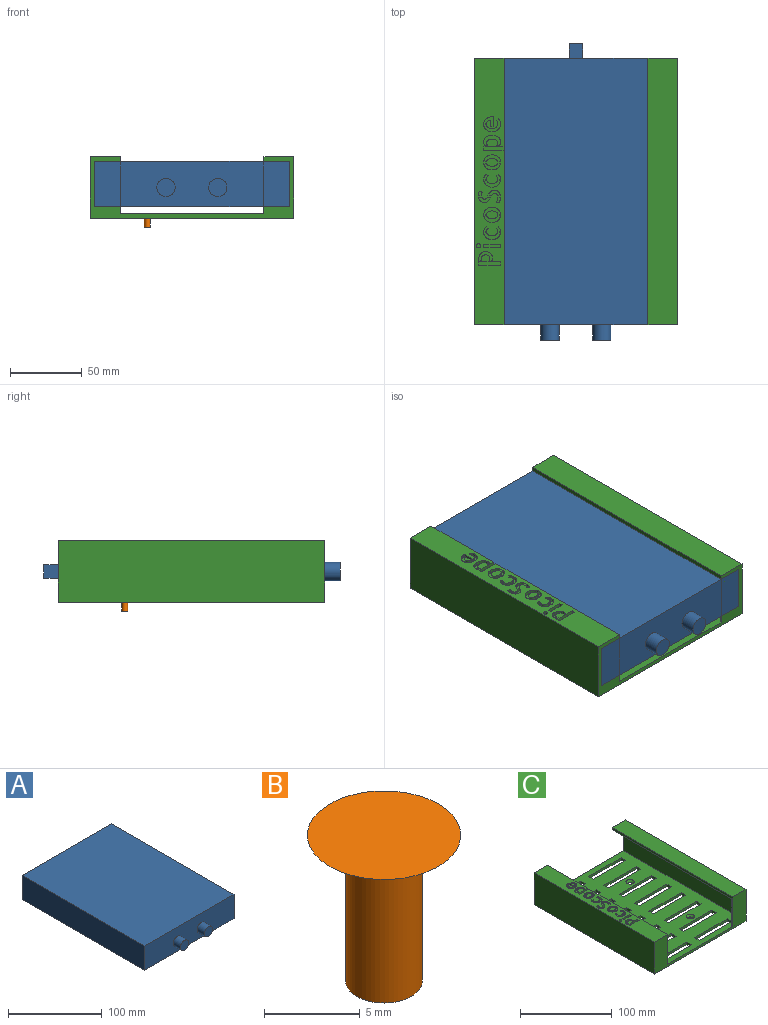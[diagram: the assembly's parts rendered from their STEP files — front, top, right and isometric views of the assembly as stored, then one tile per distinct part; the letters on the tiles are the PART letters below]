
ASSEMBLY  parts=3 mates=5
PART A: 23 faces, bbox 135x205.8x36.5 mm
  f0: plane 185x31.5mm, normal (1,0,0), area 5827.5mm2, adj f1,f3,f4,f18
  f1: plane 135x31.5mm, normal (0,1,0), area 4162.2mm2, adj f0,f2,f4,f9,f10,f11,f12,f18
  f2: plane 185x31.5mm, normal (-1,0,0), area 5827.5mm2, adj f1,f3,f4,f18
  f3: plane 135x31.5mm, normal (0,-1,0), area 3999.1mm2, adj f0,f2,f4,f5,f7,f18
  f4: plane 185x135mm, normal (0,0,1), area 24975mm2, adj f0,f1,f2,f3
  f5: cylinder r=6.35mm len=12.7mm, axis (0,1,0), area 430.9mm2, adj f3,f6
  f6: plane 12.7x12.7mm, normal (0,-1,0), area 126.7mm2, adj f5
  f7: cylinder r=6.35mm len=12.7mm, axis (0,1,0), area 430.9mm2, adj f3,f8
  f8: plane 12.7x12.7mm, normal (0,-1,0), area 126.7mm2, adj f7
  f9: plane 10x9.5mm, normal (-1,0,0), area 95mm2, adj f1,f10,f12,f13
  f10: plane 10x9.5mm, normal (0,0,1), area 95mm2, adj f1,f9,f11,f13
  f11: plane 10x9.5mm, normal (1,0,0), area 95mm2, adj f1,f10,f12,f13
  f12: plane 10x9.5mm, normal (0,0,-1), area 95mm2, adj f1,f9,f11,f13
  f13: plane 9.5x9.5mm, normal (0,1,0), area 90.2mm2, adj f9,f10,f11,f12
  f14: cylinder r=5mm len=10mm, axis (0,0,-1), area 157.1mm2, adj f18,f21
  f15: cylinder r=5mm len=10mm, axis (0,0,-1), area 157.1mm2, adj f18,f20
  f16: cylinder r=5mm len=10mm, axis (0,0,-1), area 157.1mm2, adj f18,f19
  f17: cylinder r=5mm len=10mm, axis (0,0,-1), area 157.1mm2, adj f18,f22
  f18: plane 185x135mm, normal (0,0,-1), area 24660.8mm2, adj f0,f1,f2,f3,f14,f15,f16,f17
  f19: plane 10x10mm, normal (0,0,-1), area 78.5mm2, adj f16
  f20: plane 10x10mm, normal (0,0,-1), area 78.5mm2, adj f15
  f21: plane 10x10mm, normal (0,0,-1), area 78.5mm2, adj f14
  f22: plane 10x10mm, normal (0,0,-1), area 78.5mm2, adj f17
PART B: 4 faces, bbox 8x8x9.3 mm
  f0: plane 8x8mm, normal (0,0,1), area 50.3mm2, adj f1
  f1: cone r=4mm half-angle=57deg, axis (0,0,1), area 45mm2, adj f0,f2
  f2: cylinder r=2mm len=8mm, axis (0,0,1), area 100.5mm2, adj f1,f3
  f3: plane 4x4mm, normal (0,0,-1), area 12.6mm2, adj f2
PART C: 385 faces, bbox 141.1x185x42.5 mm
  f0: plane 185x135.1mm, normal (0,0,1), area 19106.2mm2, adj f1,f4,f9,f11,f12,f13,f14,f15
  f1: plane 185x39.5mm, normal (1,0,0), area 586.5mm2, adj f0,f2,f5,f12,f13,f282,f285,f286
  f2: plane 185x20.55mm, normal (0,0,1), area 3302.4mm2, adj f1,f6,f12,f13,f78,f79,f80,f81
  f3: plane 185x141.1mm, normal (0,0,-1), area 20439.9mm2, adj f6,f7,f12,f13,f14,f15,f16,f17
  f4: plane 184x36.5mm, normal (1,0,0), area 6716mm2, adj f0,f5,f12,f383
  f5: plane 184x17.55mm, normal (0,0,-1), area 3229.2mm2, adj f1,f4,f12,f383
  f6: plane 185x42.5mm, normal (-1,0,0), area 7862.5mm2, adj f2,f3,f12,f13
  f7: plane 185x42.5mm, normal (1,0,0), area 7862.5mm2, adj f3,f8,f12,f13
  f8: plane 185x20.55mm, normal (0,0,1), area 3801.7mm2, adj f7,f9,f12,f13
  f9: plane 185x39.5mm, normal (-1,0,0), area 591.5mm2, adj f0,f8,f10,f12,f13,f384
  f10: plane 184x17.55mm, normal (0,0,-1), area 3229.2mm2, adj f9,f11,f12,f384
  f11: plane 184x36.5mm, normal (-1,0,0), area 6716mm2, adj f0,f10,f12,f384
  f12: plane 141.1x42.5mm, normal (0,1,0), area 765.6mm2, adj f0,f1,f2,f3,f4,f5,f6,f7
  f13: plane 141.1x42.5mm, normal (0,-1,0), area 2046.7mm2, adj f0,f1,f2,f3,f6,f7,f8,f9
  f14: plane 50x3mm, normal (0,-1,0), area 150mm2, adj f0,f3,f15,f16
  f15: plane 7x3mm, normal (1,0,0), area 21mm2, adj f0,f3,f14,f17
  f16: plane 7x3mm, normal (-1,0,0), area 21mm2, adj f0,f3,f14,f17
  f17: plane 50x3mm, normal (0,1,0), area 150mm2, adj f0,f3,f15,f16
  f18: plane 50x3mm, normal (0,1,0), area 150mm2, adj f0,f3,f19,f21
  f19: plane 7x3mm, normal (1,0,0), area 21mm2, adj f0,f3,f18,f20
  f20: plane 50x3mm, normal (0,-1,0), area 150mm2, adj f0,f3,f19,f21
  f21: plane 7x3mm, normal (-1,0,0), area 21mm2, adj f0,f3,f18,f20
  f22: plane 7x3mm, normal (-1,0,0), area 21mm2, adj f0,f3,f23,f24
  f23: plane 50x3mm, normal (0,-1,0), area 150mm2, adj f0,f3,f22,f25
  f24: plane 50x3mm, normal (0,1,0), area 150mm2, adj f0,f3,f22,f25
  f25: plane 7x3mm, normal (1,0,0), area 21mm2, adj f0,f3,f23,f24
  f26: plane 50x3mm, normal (0,1,0), area 150mm2, adj f0,f3,f27,f29
  f27: plane 7x3mm, normal (1,0,0), area 21mm2, adj f0,f3,f26,f28
  f28: plane 50x3mm, normal (0,-1,0), area 150mm2, adj f0,f3,f27,f29
  f29: plane 7x3mm, normal (-1,0,0), area 21mm2, adj f0,f3,f26,f28
  f30: plane 50x3mm, normal (0,-1,0), area 150mm2, adj f0,f3,f31,f32
  f31: plane 7x3mm, normal (1,0,0), area 21mm2, adj f0,f3,f30,f33
  f32: plane 7x3mm, normal (-1,0,0), area 21mm2, adj f0,f3,f30,f33
  f33: plane 50x3mm, normal (0,1,0), area 150mm2, adj f0,f3,f31,f32
  f34: plane 7x3mm, normal (-1,0,0), area 21mm2, adj f0,f3,f35,f36
  f35: plane 50x3mm, normal (0,-1,0), area 150mm2, adj f0,f3,f34,f37
  f36: plane 50x3mm, normal (0,1,0), area 150mm2, adj f0,f3,f34,f37
  f37: plane 7x3mm, normal (1,0,0), area 21mm2, adj f0,f3,f35,f36
  f38: plane 50x3mm, normal (0,1,0), area 150mm2, adj f0,f3,f39,f41
  f39: plane 7x3mm, normal (1,0,0), area 21mm2, adj f0,f3,f38,f40
  f40: plane 50x3mm, normal (0,-1,0), area 150mm2, adj f0,f3,f39,f41
  f41: plane 7x3mm, normal (-1,0,0), area 21mm2, adj f0,f3,f38,f40
  f42: plane 7x3mm, normal (-1,0,0), area 21mm2, adj f0,f3,f43,f44
  f43: plane 50x3mm, normal (0,-1,0), area 150mm2, adj f0,f3,f42,f45
  f44: plane 50x3mm, normal (0,1,0), area 150mm2, adj f0,f3,f42,f45
  f45: plane 7x3mm, normal (1,0,0), area 21mm2, adj f0,f3,f43,f44
  f46: plane 50x3mm, normal (0,-1,0), area 150mm2, adj f0,f3,f47,f48
  f47: plane 7x3mm, normal (1,0,0), area 21mm2, adj f0,f3,f46,f49
  f48: plane 7x3mm, normal (-1,0,0), area 21mm2, adj f0,f3,f46,f49
  f49: plane 50x3mm, normal (0,1,0), area 150mm2, adj f0,f3,f47,f48
  f50: plane 50x3mm, normal (0,-1,0), area 150mm2, adj f0,f3,f51,f52
  f51: plane 7x3mm, normal (1,0,0), area 21mm2, adj f0,f3,f50,f53
  f52: plane 7x3mm, normal (-1,0,0), area 21mm2, adj f0,f3,f50,f53
  f53: plane 50x3mm, normal (0,1,0), area 150mm2, adj f0,f3,f51,f52
  f54: plane 50x3mm, normal (0,-1,0), area 150mm2, adj f0,f3,f55,f56
  f55: plane 7x3mm, normal (1,0,0), area 21mm2, adj f0,f3,f54,f57
  f56: plane 7x3mm, normal (-1,0,0), area 21mm2, adj f0,f3,f54,f57
  f57: plane 50x3mm, normal (0,1,0), area 150mm2, adj f0,f3,f55,f56
  f58: plane 50x3mm, normal (0,-1,0), area 150mm2, adj f0,f3,f59,f60
  f59: plane 7x3mm, normal (1,0,0), area 21mm2, adj f0,f3,f58,f61
  f60: plane 7x3mm, normal (-1,0,0), area 21mm2, adj f0,f3,f58,f61
  f61: plane 50x3mm, normal (0,1,0), area 150mm2, adj f0,f3,f59,f60
  f62: plane 50x3mm, normal (0,-1,0), area 150mm2, adj f0,f3,f63,f64
  f63: plane 7x3mm, normal (1,0,0), area 21mm2, adj f0,f3,f62,f65
  f64: plane 7x3mm, normal (-1,0,0), area 21mm2, adj f0,f3,f62,f65
  f65: plane 50x3mm, normal (0,1,0), area 150mm2, adj f0,f3,f63,f64
  f66: plane 7x3mm, normal (1,0,0), area 21mm2, adj f0,f3,f67,f68
  f67: plane 50x3mm, normal (0,1,0), area 150mm2, adj f0,f3,f66,f69
  f68: plane 50x3mm, normal (0,-1,0), area 150mm2, adj f0,f3,f66,f69
  f69: plane 7x3mm, normal (-1,0,0), area 21mm2, adj f0,f3,f67,f68
  f70: plane 7x3mm, normal (1,0,0), area 21mm2, adj f0,f3,f71,f72
  f71: plane 50x3mm, normal (0,1,0), area 150mm2, adj f0,f3,f70,f73
  f72: plane 50x3mm, normal (0,-1,0), area 150mm2, adj f0,f3,f70,f73
  f73: plane 7x3mm, normal (-1,0,0), area 21mm2, adj f0,f3,f71,f72
  f74: plane 7x3mm, normal (1,0,0), area 21mm2, adj f0,f3,f75,f76
  f75: plane 50x3mm, normal (0,1,0), area 150mm2, adj f0,f3,f74,f77
  f76: plane 50x3mm, normal (0,-1,0), area 150mm2, adj f0,f3,f74,f77
  f77: plane 7x3mm, normal (-1,0,0), area 21mm2, adj f0,f3,f75,f76
  f78: extruded ~2.2x2mm, area 4.5mm2, adj f2,f79,f93,f94
  f79: extruded ~2.2x2mm, area 4.5mm2, adj f2,f78,f80,f94
  f80: extruded ~2x1.81mm, area 4.1mm2, adj f2,f79,f81,f94
  f81: extruded ~2x1.53mm, area 4mm2, adj f2,f80,f82,f94
  f82: extruded ~2.02x2mm, area 4.2mm2, adj f2,f81,f83,f94
  f83: plane 2x1.95mm, normal (0,-1,0), area 3.9mm2, adj f2,f82,f84,f94
  f84: extruded ~2x0.95mm, area 2.1mm2, adj f2,f83,f85,f94
  f85: extruded ~2x0.88mm, area 2.3mm2, adj f2,f84,f86,f94
  f86: extruded ~2x1.2mm, area 2.6mm2, adj f2,f85,f87,f94
  f87: extruded ~2x1.42mm, area 2.9mm2, adj f2,f86,f88,f94
  f88: extruded ~2.55x2mm, area 5.3mm2, adj f2,f87,f89,f94
  f89: extruded ~2x1.63mm, area 4.3mm2, adj f2,f88,f90,f94
  f90: plane 2x1.89mm, normal (0,-1,0), area 3.8mm2, adj f2,f89,f91,f94
  f91: extruded ~2x1.98mm, area 4.1mm2, adj f2,f90,f92,f94
  f92: extruded ~2x1.54mm, area 4mm2, adj f2,f91,f93,f94
  f93: extruded ~2x1.78mm, area 4.1mm2, adj f2,f78,f92,f94
  f94: plane 11.6x4.84mm, normal (0,0,1), area 30.6mm2, adj f78,f79,f80,f81,f82,f83,f84,f85
  f95: extruded ~2.03x2mm, area 4.2mm2, adj f2,f96,f110,f111
  f96: plane 2x1.91mm, normal (0,1,0), area 3.8mm2, adj f2,f95,f97,f111
  f97: extruded ~2x0.96mm, area 2.1mm2, adj f2,f96,f98,f111
  f98: extruded ~2x0.87mm, area 2.3mm2, adj f2,f97,f99,f111
  f99: extruded ~2x1.19mm, area 2.6mm2, adj f2,f98,f100,f111
  f100: extruded ~2x1.41mm, area 2.9mm2, adj f2,f99,f101,f111
  f101: extruded ~2.54x2mm, area 5.3mm2, adj f2,f100,f102,f111
  f102: extruded ~2x1.66mm, area 4.3mm2, adj f2,f101,f103,f111
  f103: plane 2x1.95mm, normal (0,1,0), area 3.9mm2, adj f2,f102,f104,f111
  f104: extruded ~2x1.99mm, area 4.2mm2, adj f2,f103,f105,f111
  f105: extruded ~2x1.55mm, area 4mm2, adj f2,f104,f106,f111
  f106: extruded ~2x1.79mm, area 4.1mm2, adj f2,f105,f107,f111
  f107: extruded ~2.21x2mm, area 4.5mm2, adj f2,f106,f108,f111
  f108: extruded ~2.22x2mm, area 4.5mm2, adj f2,f107,f109,f111
  f109: extruded ~2x1.82mm, area 4.1mm2, adj f2,f108,f110,f111
  f110: extruded ~2x1.54mm, area 4mm2, adj f2,f95,f109,f111
  f111: plane 11.62x4.88mm, normal (0,0,1), area 30.9mm2, adj f95,f96,f97,f98,f99,f100,f101,f102
  f112: extruded ~2.18x2mm, area 4.4mm2, adj f2,f113,f127,f128
  f113: extruded ~2.2x2mm, area 4.5mm2, adj f2,f112,f114,f128
  f114: extruded ~2x1.82mm, area 4.1mm2, adj f2,f113,f115,f128
  f115: extruded ~2x1.53mm, area 4mm2, adj f2,f114,f116,f128
  f116: extruded ~2.02x2mm, area 4.2mm2, adj f2,f115,f117,f128
  f117: plane 2.02x2mm, normal (0,-1,0), area 4mm2, adj f2,f116,f118,f128
  f118: extruded ~2x0.95mm, area 2.1mm2, adj f2,f117,f119,f128
  f119: extruded ~2x0.85mm, area 2.2mm2, adj f2,f118,f120,f128
  f120: extruded ~2x1.17mm, area 2.5mm2, adj f2,f119,f121,f128
  f121: extruded ~2x1.41mm, area 2.8mm2, adj f2,f120,f122,f128
  f122: extruded ~2.49x2mm, area 5.2mm2, adj f2,f121,f123,f128
  f123: extruded ~2x1.63mm, area 4.2mm2, adj f2,f122,f124,f128
  f124: plane 2x1.98mm, normal (0,-1,0), area 4mm2, adj f2,f123,f125,f128
  f125: extruded ~2x1.98mm, area 4.2mm2, adj f2,f124,f126,f128
  f126: extruded ~2x1.54mm, area 4mm2, adj f2,f125,f127,f128
  f127: extruded ~2x1.79mm, area 4.1mm2, adj f2,f112,f126,f128
  f128: plane 11.6x4.84mm, normal (0,0,1), area 30.9mm2, adj f112,f113,f114,f115,f116,f117,f118,f119
  f129: extruded ~2x1.25mm, area 2.6mm2, adj f2,f130,f134,f135
  f130: plane 2.02x2mm, normal (0,1,0), area 4mm2, adj f2,f129,f131,f135
  f131: extruded ~2x1.79mm, area 3.7mm2, adj f2,f130,f132,f135
  f132: extruded ~2x1.36mm, area 3.7mm2, adj f2,f131,f133,f135
  f133: plane 2x1.32mm, normal (0.57,-0.82,0), area 3.2mm2, adj f2,f132,f134,f135
  f134: extruded ~2x0.99mm, area 2.4mm2, adj f2,f129,f133,f135
  f135: plane 3.15x3.01mm, normal (0,0,1), area 5.8mm2, adj f129,f130,f131,f132,f133,f134
  f136: extruded ~2x1.89mm, area 3.9mm2, adj f2,f137,f157,f158
  f137: plane 2x1.04mm, normal (1,0,0), area 2.1mm2, adj f2,f136,f138,f158
  f138: plane 2x1.85mm, normal (0,1,0), area 3.7mm2, adj f2,f137,f139,f158
  f139: plane 2x1mm, normal (-1,0,0), area 2mm2, adj f2,f138,f140,f158
  f140: extruded ~2x1.51mm, area 3.1mm2, adj f2,f139,f141,f158
  f141: extruded ~2x0.89mm, area 2.3mm2, adj f2,f140,f142,f158
  f142: extruded ~2x0.91mm, area 2mm2, adj f2,f141,f143,f158
  f143: extruded ~2x0.85mm, area 1.7mm2, adj f2,f142,f144,f158
  f144: extruded ~2x1.54mm, area 3.1mm2, adj f2,f143,f145,f158
  f145: extruded ~2x0.97mm, area 2.3mm2, adj f2,f144,f146,f158
  f146: extruded ~2x0.8mm, area 1.9mm2, adj f2,f145,f147,f158
  f147: extruded ~2x0.89mm, area 1.8mm2, adj f2,f146,f148,f158
  f148: plane 2x1.4mm, normal (1,0,0), area 2.8mm2, adj f2,f147,f149,f158
  f149: plane 2x1.79mm, normal (0,1,0), area 3.6mm2, adj f2,f148,f150,f158
  f150: plane 2x0.98mm, normal (-1,0,0), area 2mm2, adj f2,f149,f151,f158
  f151: extruded ~2.16x2mm, area 4.4mm2, adj f2,f150,f152,f158
  f152: extruded ~2x1.67mm, area 3.9mm2, adj f2,f151,f153,f158
  f153: extruded ~2x1.56mm, area 3.8mm2, adj f2,f152,f154,f158
  f154: extruded ~2.06x2mm, area 4.2mm2, adj f2,f153,f155,f158
  f155: extruded ~2x1.95mm, area 4mm2, adj f2,f154,f156,f158
  f156: extruded ~2x1.47mm, area 3.8mm2, adj f2,f155,f157,f158
  f157: extruded ~2x1.68mm, area 3.8mm2, adj f2,f136,f156,f158
  f158: plane 9.58x6.27mm, normal (0,0,1), area 29.6mm2, adj f136,f137,f138,f139,f140,f141,f142,f143
  f159: plane 2.48x2mm, normal (-1,0,0), area 5mm2, adj f2,f160,f162,f163
  f160: plane 11.47x2mm, normal (0,-1,0), area 22.9mm2, adj f2,f159,f161,f163
  f161: plane 2.48x2mm, normal (1,0,0), area 5mm2, adj f2,f160,f162,f163
  f162: plane 11.47x2mm, normal (0,1,0), area 22.9mm2, adj f2,f159,f161,f163
  f163: plane 11.47x2.48mm, normal (0,0,1), area 28.5mm2, adj f159,f160,f161,f162
  f164: extruded ~2x1.03mm, area 2.3mm2, adj f2,f165,f171,f172
  f165: extruded ~2x1.04mm, area 2.3mm2, adj f2,f164,f166,f172
  f166: extruded ~2x1.04mm, area 2.3mm2, adj f2,f165,f167,f172
  f167: extruded ~2x1.02mm, area 2.3mm2, adj f2,f166,f168,f172
  f168: extruded ~2x1.04mm, area 2.3mm2, adj f2,f167,f169,f172
  f169: extruded ~2x1.02mm, area 2.3mm2, adj f2,f168,f170,f172
  f170: extruded ~2x1.03mm, area 2.3mm2, adj f2,f169,f171,f172
  f171: extruded ~2x1.04mm, area 2.3mm2, adj f2,f164,f170,f172
  f172: plane 2.91x2.91mm, normal (0,0,1), area 6.7mm2, adj f164,f165,f166,f167,f168,f169,f170,f171
  f173: extruded ~2x0.84mm, area 2.2mm2, adj f2,f174,f178,f179
  f174: plane 2x1.32mm, normal (-0.64,-0.77,0), area 3.4mm2, adj f2,f173,f175,f179
  f175: extruded ~2x1.46mm, area 3.8mm2, adj f2,f174,f176,f179
  f176: extruded ~2x1.92mm, area 4mm2, adj f2,f175,f177,f179
  f177: plane 2x1.95mm, normal (0,1,0), area 3.9mm2, adj f2,f176,f178,f179
  f178: extruded ~2x1.44mm, area 3mm2, adj f2,f173,f177,f179
  f179: plane 3.38x3.01mm, normal (0,0,1), area 6mm2, adj f173,f174,f175,f176,f177,f178
  f180: extruded ~2x1.37mm, area 3mm2, adj f2,f181,f192,f193
  f181: plane 2.38x2mm, normal (0,1,0), area 4.8mm2, adj f2,f180,f182,f193
  f182: extruded ~2x1.2mm, area 3mm2, adj f2,f181,f183,f193
  f183: extruded ~2x1.18mm, area 2.6mm2, adj f2,f182,f184,f193
  f184: extruded ~2.22x2mm, area 6.1mm2, adj f2,f183,f185,f193
  f185: plane 2x1.95mm, normal (0,1,0), area 3.9mm2, adj f2,f184,f186,f193
  f186: extruded ~2x1.67mm, area 3.5mm2, adj f2,f185,f187,f193
  f187: extruded ~2x1.23mm, area 3.1mm2, adj f2,f186,f188,f193
  f188: extruded ~2x1.25mm, area 3mm2, adj f2,f187,f189,f193
  f189: extruded ~2x1.42mm, area 2.9mm2, adj f2,f188,f190,f193
  f190: extruded ~2x1.77mm, area 3.6mm2, adj f2,f189,f191,f193
  f191: extruded ~2x1.21mm, area 3.1mm2, adj f2,f190,f192,f193
  f192: extruded ~2x1.27mm, area 3.1mm2, adj f2,f180,f191,f193
  f193: plane 8.61x3.95mm, normal (0,0,1), area 20mm2, adj f180,f181,f182,f183,f184,f185,f186,f187
  f194: extruded ~2x0.72mm, area 1.6mm2, adj f2,f195,f205,f206
  f195: plane 2x1.75mm, normal (0.24,0.97,0), area 3.6mm2, adj f2,f194,f196,f206
  f196: extruded ~2x0.83mm, area 2mm2, adj f2,f195,f197,f206
  f197: extruded ~2x1.01mm, area 2.1mm2, adj f2,f196,f198,f206
  f198: extruded ~2x1.05mm, area 2.1mm2, adj f2,f197,f199,f206
  f199: extruded ~2x1.01mm, area 2mm2, adj f2,f198,f200,f206
  f200: plane 2x0.04mm, normal (-1,0,0), area 0.1mm2, adj f2,f199,f201,f206
  f201: plane 2x1.93mm, normal (0,-1,0), area 3.9mm2, adj f2,f200,f202,f206
  f202: plane 2x0.06mm, normal (1,0,0), area 0.1mm2, adj f2,f201,f203,f206
  f203: extruded ~2x0.88mm, area 1.8mm2, adj f2,f202,f204,f206
  f204: extruded ~2x0.94mm, area 1.9mm2, adj f2,f203,f205,f206
  f205: extruded ~2x0.91mm, area 1.9mm2, adj f2,f194,f204,f206
  f206: plane 3.93x2.83mm, normal (0,0,1), area 7.5mm2, adj f194,f195,f196,f197,f198,f199,f200,f201
  f207: extruded ~2x1.61mm, area 3.3mm2, adj f2,f208,f220,f221
  f208: extruded ~2x1.61mm, area 3.3mm2, adj f2,f207,f209,f221
  f209: extruded ~2x1.18mm, area 3mm2, adj f2,f208,f210,f221
  f210: extruded ~2x1.22mm, area 3mm2, adj f2,f209,f211,f221
  f211: extruded ~2x1.34mm, area 3mm2, adj f2,f210,f212,f221
  f212: plane 2.32x2mm, normal (0,-1,0), area 4.6mm2, adj f2,f211,f213,f221
  f213: extruded ~2x1.08mm, area 2.8mm2, adj f2,f212,f214,f221
  f214: extruded ~2x1.28mm, area 2.8mm2, adj f2,f213,f215,f221
  f215: extruded ~2x1.13mm, area 2.5mm2, adj f2,f214,f216,f221
  f216: extruded ~2x1.08mm, area 2.7mm2, adj f2,f215,f217,f221
  f217: plane 2.14x2mm, normal (0,-1,0), area 4.3mm2, adj f2,f216,f218,f221
  f218: extruded ~2x1.48mm, area 3.1mm2, adj f2,f217,f219,f221
  f219: extruded ~2x1.22mm, area 3mm2, adj f2,f218,f220,f221
  f220: extruded ~2x1.25mm, area 3mm2, adj f2,f207,f219,f221
  f221: plane 8.51x3.83mm, normal (0,0,1), area 19.7mm2, adj f207,f208,f209,f210,f211,f212,f213,f214
  f222: extruded ~2x0.24mm, area 0.6mm2, adj f2,f223,f232,f233
  f223: extruded ~2x0.2mm, area 0.5mm2, adj f2,f222,f224,f233
  f224: extruded ~2x0.46mm, area 1mm2, adj f2,f223,f225,f233
  f225: extruded ~2x0.59mm, area 1.3mm2, adj f2,f224,f226,f233
  f226: extruded ~2x0.58mm, area 1.3mm2, adj f2,f225,f227,f233
  f227: extruded ~2x1.5mm, area 3.2mm2, adj f2,f226,f228,f233
  f228: extruded ~2x1.82mm, area 3.7mm2, adj f2,f227,f229,f233
  f229: plane 2.05x2mm, normal (0,1,0), area 4.1mm2, adj f2,f228,f230,f233
  f230: extruded ~2x1.04mm, area 2.1mm2, adj f2,f229,f231,f233
  f231: extruded ~2x0.67mm, area 1.4mm2, adj f2,f230,f232,f233
  f232: extruded ~2x0.41mm, area 0.9mm2, adj f2,f222,f231,f233
  f233: plane 3.32x2.56mm, normal (0,0,1), area 6mm2, adj f222,f223,f224,f225,f226,f227,f228,f229
  f234: extruded ~2.03x2mm, area 4.2mm2, adj f2,f235,f249,f250
  f235: plane 2x1.91mm, normal (0,1,0), area 3.8mm2, adj f2,f234,f236,f250
  f236: extruded ~2x0.96mm, area 2.1mm2, adj f2,f235,f237,f250
  f237: extruded ~2x0.87mm, area 2.3mm2, adj f2,f236,f238,f250
  f238: extruded ~2x1.19mm, area 2.6mm2, adj f2,f237,f239,f250
  f239: extruded ~2x1.41mm, area 2.9mm2, adj f2,f238,f240,f250
  f240: extruded ~2.54x2mm, area 5.3mm2, adj f2,f239,f241,f250
  f241: extruded ~2x1.66mm, area 4.3mm2, adj f2,f240,f242,f250
  f242: plane 2x1.95mm, normal (0,1,0), area 3.9mm2, adj f2,f241,f243,f250
  f243: extruded ~2x1.99mm, area 4.2mm2, adj f2,f242,f244,f250
  f244: extruded ~2x1.55mm, area 4mm2, adj f2,f243,f245,f250
  f245: extruded ~2x1.79mm, area 4.1mm2, adj f2,f244,f246,f250
  f246: extruded ~2.21x2mm, area 4.5mm2, adj f2,f245,f247,f250
  f247: extruded ~2.22x2mm, area 4.5mm2, adj f2,f246,f248,f250
  f248: extruded ~2x1.82mm, area 4.1mm2, adj f2,f247,f249,f250
  f249: extruded ~2x1.54mm, area 4mm2, adj f2,f234,f248,f250
  f250: plane 11.62x4.88mm, normal (0,0,1), area 30.9mm2, adj f234,f235,f236,f237,f238,f239,f240,f241
  f251: extruded ~2.18x2mm, area 4.4mm2, adj f2,f252,f266,f267
  f252: extruded ~2.2x2mm, area 4.5mm2, adj f2,f251,f253,f267
  f253: extruded ~2x1.82mm, area 4.1mm2, adj f2,f252,f254,f267
  f254: extruded ~2x1.53mm, area 4mm2, adj f2,f253,f255,f267
  f255: extruded ~2.02x2mm, area 4.2mm2, adj f2,f254,f256,f267
  f256: plane 2.02x2mm, normal (0,-1,0), area 4mm2, adj f2,f255,f257,f267
  f257: extruded ~2x0.95mm, area 2.1mm2, adj f2,f256,f258,f267
  f258: extruded ~2x0.85mm, area 2.2mm2, adj f2,f257,f259,f267
  f259: extruded ~2x1.17mm, area 2.5mm2, adj f2,f258,f260,f267
  f260: extruded ~2x1.41mm, area 2.8mm2, adj f2,f259,f261,f267
  f261: extruded ~2.49x2mm, area 5.2mm2, adj f2,f260,f262,f267
  f262: extruded ~2x1.63mm, area 4.2mm2, adj f2,f261,f263,f267
  f263: plane 2x1.98mm, normal (0,-1,0), area 4mm2, adj f2,f262,f264,f267
  f264: extruded ~2x1.98mm, area 4.2mm2, adj f2,f263,f265,f267
  f265: extruded ~2x1.54mm, area 4mm2, adj f2,f264,f266,f267
  f266: extruded ~2x1.79mm, area 4.1mm2, adj f2,f251,f265,f267
  f267: plane 11.6x4.84mm, normal (0,0,1), area 30.9mm2, adj f251,f252,f253,f254,f255,f256,f257,f258
  f268: extruded ~2x1.25mm, area 2.6mm2, adj f2,f269,f273,f274
  f269: plane 2.02x2mm, normal (0,1,0), area 4mm2, adj f2,f268,f270,f274
  f270: extruded ~2x1.79mm, area 3.7mm2, adj f2,f269,f271,f274
  f271: extruded ~2x1.36mm, area 3.7mm2, adj f2,f270,f272,f274
  f272: plane 2x1.32mm, normal (0.57,-0.82,0), area 3.2mm2, adj f2,f271,f273,f274
  f273: extruded ~2x0.99mm, area 2.4mm2, adj f2,f268,f272,f274
  f274: plane 3.15x3.01mm, normal (0,0,1), area 5.8mm2, adj f268,f269,f270,f271,f272,f273
  f275: extruded ~2x0.84mm, area 2.2mm2, adj f2,f276,f280,f281
  f276: plane 2x1.32mm, normal (-0.64,-0.77,0), area 3.4mm2, adj f2,f275,f277,f281
  f277: extruded ~2x1.46mm, area 3.8mm2, adj f2,f276,f278,f281
  f278: extruded ~2x1.92mm, area 4mm2, adj f2,f277,f279,f281
  f279: plane 2x1.95mm, normal (0,1,0), area 3.9mm2, adj f2,f278,f280,f281
  f280: extruded ~2x1.44mm, area 3mm2, adj f2,f275,f279,f281
  f281: plane 3.38x3.01mm, normal (0,0,1), area 6mm2, adj f275,f276,f277,f278,f279,f280
  f282: plane 12.87x2mm, normal (0,-1,0), area 25.7mm2, adj f1,f2,f283,f286
  f283: plane 2x1.16mm, normal (0.22,-0.98,0), area 2.4mm2, adj f2,f282,f284,f286
  f284: plane 2.22x2mm, normal (1,0,0), area 4.4mm2, adj f2,f283,f285,f286
  f285: plane 14.02x2mm, normal (0,1,0), area 28mm2, adj f1,f2,f284,f286
  f286: plane 14.02x2.48mm, normal (0,0,1), area 34.6mm2, adj f1,f282,f283,f284,f285
  f287: extruded ~2x1.98mm, area 4.2mm2, adj f2,f288,f299,f300
  f288: plane 2x1.91mm, normal (0,1,0), area 3.8mm2, adj f2,f287,f289,f300
  f289: extruded ~2x1mm, area 2.1mm2, adj f2,f288,f290,f300
  f290: extruded ~2x0.78mm, area 2.1mm2, adj f2,f289,f291,f300
  f291: extruded ~2x0.91mm, area 2.1mm2, adj f2,f290,f292,f300
  f292: extruded ~2x1.02mm, area 2.1mm2, adj f2,f291,f293,f300
  f293: plane 4.7x2mm, normal (1,0,0), area 9.4mm2, adj f2,f292,f294,f300
  f294: plane 2x1.79mm, normal (0,1,0), area 3.6mm2, adj f2,f293,f295,f300
  f295: plane 6.98x2mm, normal (-1,0,0), area 14mm2, adj f2,f294,f296,f300
  f296: extruded ~2x0.98mm, area 2mm2, adj f2,f295,f297,f300
  f297: extruded ~2.08x2mm, area 4.2mm2, adj f2,f296,f298,f300
  f298: extruded ~2x1.77mm, area 4.1mm2, adj f2,f297,f299,f300
  f299: extruded ~2x1.52mm, area 4mm2, adj f2,f287,f298,f300
  f300: plane 7.04x6.67mm, normal (0,0,1), area 24.4mm2, adj f287,f288,f289,f290,f291,f292,f293,f294
  f301: extruded ~2x0.56mm, area 1.1mm2, adj f2,f302,f324,f325
  f302: extruded ~2x1.45mm, area 3mm2, adj f2,f301,f303,f325
  f303: extruded ~2x1.01mm, area 2.6mm2, adj f2,f302,f304,f325
  f304: extruded ~2x1.18mm, area 2.7mm2, adj f2,f303,f305,f325
  f305: extruded ~2x1.48mm, area 3mm2, adj f2,f304,f306,f325
  f306: extruded ~2x1.08mm, area 2.2mm2, adj f2,f305,f307,f325
  f307: extruded ~2x1.23mm, area 2.6mm2, adj f2,f306,f308,f325
  f308: extruded ~2x1.07mm, area 2.6mm2, adj f2,f307,f309,f325
  f309: extruded ~2x1.24mm, area 2.8mm2, adj f2,f308,f310,f325
  f310: plane 2x1.95mm, normal (0,-1,0), area 3.9mm2, adj f2,f309,f311,f325
  f311: extruded ~2x1.86mm, area 3.9mm2, adj f2,f310,f312,f325
  f312: extruded ~2x1.52mm, area 4mm2, adj f2,f311,f313,f325
  f313: extruded ~2x1.82mm, area 4.2mm2, adj f2,f312,f314,f325
  f314: extruded ~2.2x2mm, area 4.5mm2, adj f2,f313,f315,f325
  f315: extruded ~2.28x2mm, area 4.7mm2, adj f2,f314,f316,f325
  f316: extruded ~2x1.85mm, area 4.3mm2, adj f2,f315,f317,f325
  f317: extruded ~2x1.67mm, area 4.2mm2, adj f2,f316,f318,f325
  f318: extruded ~2.1x2mm, area 4.3mm2, adj f2,f317,f319,f325
  f319: extruded ~2.28x2mm, area 4.7mm2, adj f2,f318,f320,f325
  f320: extruded ~2x1.57mm, area 4.1mm2, adj f2,f319,f321,f325
  f321: plane 2x1.36mm, normal (0.55,-0.84,0), area 3.3mm2, adj f2,f320,f322,f325
  f322: extruded ~2x0.66mm, area 1.7mm2, adj f2,f321,f323,f325
  f323: extruded ~2x0.75mm, area 1.7mm2, adj f2,f322,f324,f325
  f324: extruded ~2x0.71mm, area 1.5mm2, adj f2,f301,f323,f325
  f325: plane 11.68x9.11mm, normal (0,0,1), area 36.3mm2, adj f301,f302,f303,f304,f305,f306,f307,f308
  f326: extruded ~2.09x2mm, area 4.2mm2, adj f2,f327,f351,f352
  f327: extruded ~2x1.67mm, area 3.7mm2, adj f2,f326,f328,f352
  f328: extruded ~2x1.12mm, area 3.1mm2, adj f2,f327,f329,f352
  f329: extruded ~2x1.29mm, area 2.9mm2, adj f2,f328,f330,f352
  f330: extruded ~2x1.36mm, area 2.8mm2, adj f2,f329,f331,f352
  f331: extruded ~2x1.18mm, area 2.4mm2, adj f2,f330,f332,f352
  f332: extruded ~2x1.04mm, area 2.2mm2, adj f2,f331,f333,f352
  f333: plane 2.16x2mm, normal (0,1,0), area 4.3mm2, adj f2,f332,f334,f352
  f334: extruded ~2x0.78mm, area 2mm2, adj f2,f333,f335,f352
  f335: extruded ~2x0.97mm, area 2mm2, adj f2,f334,f336,f352
  f336: extruded ~2x1.11mm, area 2.3mm2, adj f2,f335,f337,f352
  f337: extruded ~2x0.87mm, area 2.4mm2, adj f2,f336,f338,f352
  f338: extruded ~2x1.26mm, area 2.7mm2, adj f2,f337,f339,f352
  f339: extruded ~2x1.51mm, area 3mm2, adj f2,f338,f340,f352
  f340: extruded ~2x1.54mm, area 3.1mm2, adj f2,f339,f341,f352
  f341: extruded ~2x1.24mm, area 2.7mm2, adj f2,f340,f342,f352
  f342: extruded ~2x0.85mm, area 2.4mm2, adj f2,f341,f343,f352
  f343: extruded ~2x1.11mm, area 2.3mm2, adj f2,f342,f344,f352
  f344: extruded ~2x1.65mm, area 3.8mm2, adj f2,f343,f345,f352
  f345: plane 2.12x2mm, normal (0,1,0), area 4.2mm2, adj f2,f344,f346,f352
  f346: extruded ~2x1.11mm, area 2.4mm2, adj f2,f345,f347,f352
  f347: extruded ~2x1.35mm, area 2.7mm2, adj f2,f346,f348,f352
  f348: extruded ~2x1.98mm, area 4.1mm2, adj f2,f347,f349,f352
  f349: extruded ~2x1.4mm, area 3.9mm2, adj f2,f348,f350,f352
  f350: extruded ~2x1.92mm, area 4.2mm2, adj f2,f349,f351,f352
  f351: extruded ~2.25x2mm, area 4.5mm2, adj f2,f326,f350,f352
  f352: plane 11.68x6.96mm, normal (0,0,1), area 40.8mm2, adj f326,f327,f328,f329,f330,f331,f332,f333
  f353: extruded ~2.2x2mm, area 4.5mm2, adj f2,f354,f368,f369
  f354: extruded ~2.2x2mm, area 4.5mm2, adj f2,f353,f355,f369
  f355: extruded ~2x1.81mm, area 4.1mm2, adj f2,f354,f356,f369
  f356: extruded ~2x1.53mm, area 4mm2, adj f2,f355,f357,f369
  f357: extruded ~2.02x2mm, area 4.2mm2, adj f2,f356,f358,f369
  f358: plane 2x1.95mm, normal (0,-1,0), area 3.9mm2, adj f2,f357,f359,f369
  f359: extruded ~2x0.95mm, area 2.1mm2, adj f2,f358,f360,f369
  f360: extruded ~2x0.88mm, area 2.3mm2, adj f2,f359,f361,f369
  f361: extruded ~2x1.2mm, area 2.6mm2, adj f2,f360,f362,f369
  f362: extruded ~2x1.42mm, area 2.9mm2, adj f2,f361,f363,f369
  f363: extruded ~2.55x2mm, area 5.3mm2, adj f2,f362,f364,f369
  f364: extruded ~2x1.63mm, area 4.3mm2, adj f2,f363,f365,f369
  f365: plane 2x1.89mm, normal (0,-1,0), area 3.8mm2, adj f2,f364,f366,f369
  f366: extruded ~2x1.98mm, area 4.1mm2, adj f2,f365,f367,f369
  f367: extruded ~2x1.54mm, area 4mm2, adj f2,f366,f368,f369
  f368: extruded ~2x1.78mm, area 4.1mm2, adj f2,f353,f367,f369
  f369: plane 11.6x4.84mm, normal (0,0,1), area 30.6mm2, adj f353,f354,f355,f356,f357,f358,f359,f360
  f370: plane 2.44x2mm, normal (1,0,0), area 4.9mm2, adj f2,f371,f373,f374
  f371: plane 14.99x2mm, normal (0,1,0), area 30mm2, adj f2,f370,f372,f374
  f372: plane 2.44x2mm, normal (-1,0,0), area 4.9mm2, adj f2,f371,f373,f374
  f373: plane 14.99x2mm, normal (0,-1,0), area 30mm2, adj f2,f370,f372,f374
  f374: plane 14.99x2.44mm, normal (0,0,1), area 36.6mm2, adj f370,f371,f372,f373
  f375: cylinder r=2.25mm len=4.5mm, axis (0,0,1), area 10.9mm2, adj f3,f376
  f376: cone r=2.25mm half-angle=45deg, axis (0,0,1), area 66.7mm2, adj f0,f375
  f377: cylinder r=2.25mm len=4.5mm, axis (0,0,1), area 10.9mm2, adj f3,f378
  f378: cone r=2.25mm half-angle=45deg, axis (0,0,1), area 66.7mm2, adj f0,f377
  f379: cylinder r=2.25mm len=4.5mm, axis (0,0,1), area 10.9mm2, adj f3,f380
  f380: cone r=2.25mm half-angle=45deg, axis (0,0,1), area 66.7mm2, adj f0,f379
  f381: cylinder r=2.25mm len=4.5mm, axis (0,0,1), area 10.9mm2, adj f3,f382
  f382: cone r=2.25mm half-angle=45deg, axis (0,0,1), area 66.7mm2, adj f0,f381
  f383: plane 36.5x17.55mm, normal (0,1,0), area 640.6mm2, adj f0,f1,f4,f5
  f384: plane 36.5x17.55mm, normal (0,1,0), area 640.6mm2, adj f0,f9,f10,f11
PLACE A t=(-20.66,30.85,51.13)mm
PLACE B rot(axis=(-0.84,0,0.54),0deg) t=(-51.61,77.1,51.13)mm
PLACE C t=(-20.61,-61.65,48.13)mm fixed
MATE planar C.f0 <-> A.f14  axis (0,0,1) through (-20.61,31.02,51.13)mm
MATE planar A.f1 <-> C.f12  axis (0,1,0) through (-20.66,123.35,71.94)mm
MATE planar A.f2 <-> C.f4  axis (-1,0,0) through (-88.16,30.85,71.88)mm
MATE planar B.f1 <-> C.f0  axis (0,0,1) through (-51.61,77.1,51.13)mm
MATE cylindrical C.f382 <-> B.f1  axis (0,0,1) through (-51.61,77.1,48.52)mm
